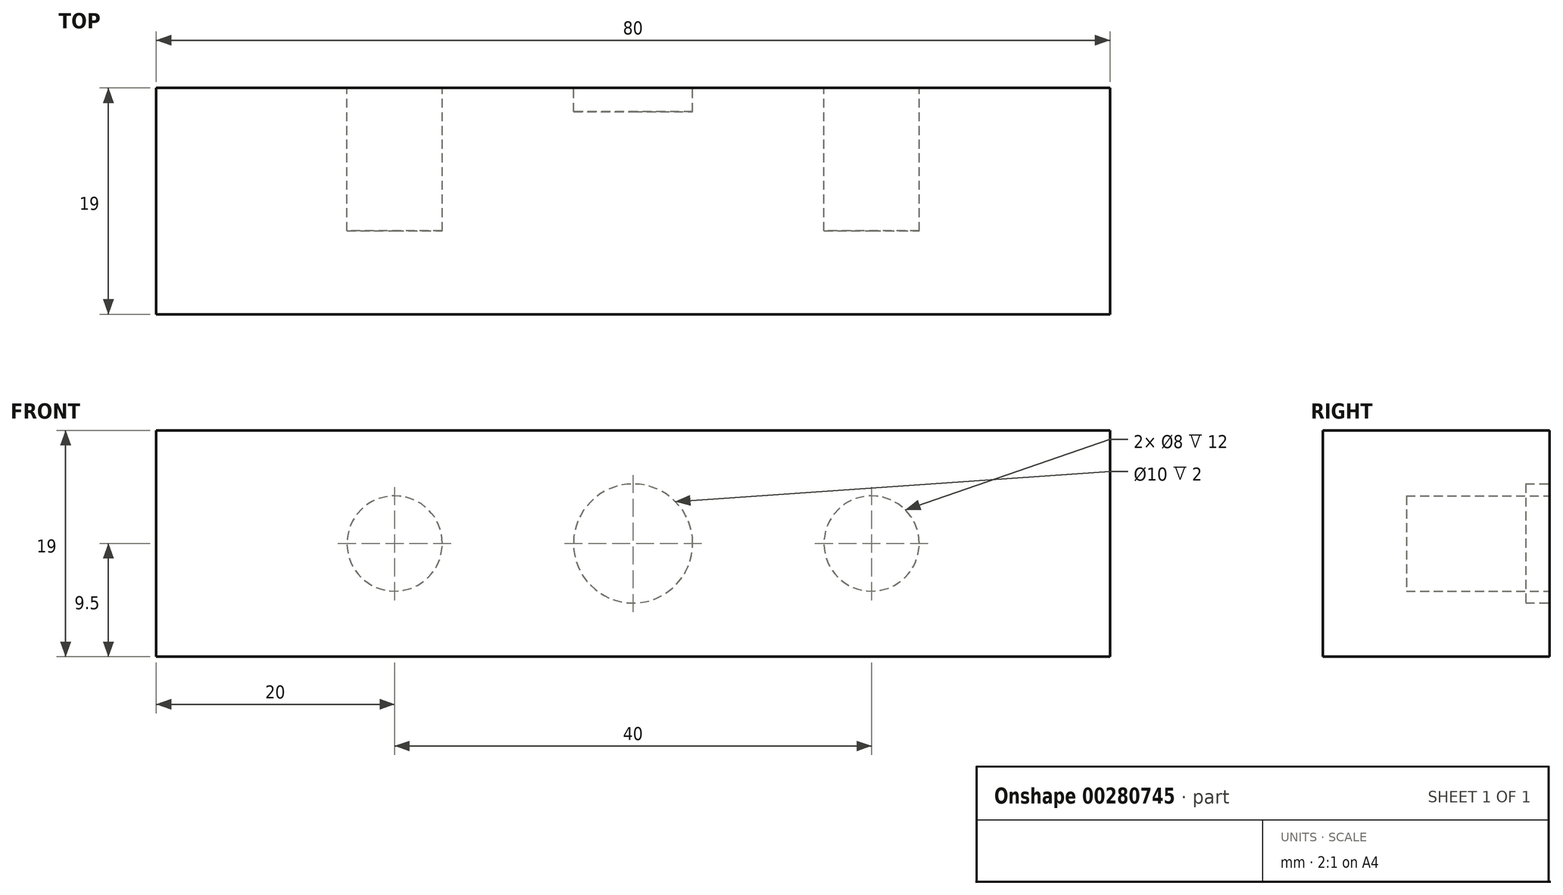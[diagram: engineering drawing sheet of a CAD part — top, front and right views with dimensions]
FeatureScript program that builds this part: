
annotation { "Feature Type Name" : "Feature", "Feature Type Description" : "" }
export const myFeature = defineFeature(function(context is Context, id is Id, definition is map)
    precondition{}
    {
        {
            var Q0;
            Q0=qCreatedBy(makeId("Top.planeOp"),FACE);
            var sketch = newSketch(context, id + "F0", { "sketchPlane" : qUnion([Q0])});
            skLineSegment(sketch, "E0.bottom", {"start": v(40, -9.5) * mm, "end": v(-40, -9.5) * mm});
            skLineSegment(sketch, "E0.top", {"start": v(40, 9.5) * mm, "end": v(-40, 9.5) * mm});
            skLineSegment(sketch, "E0.left", {"start": v(40, -9.5) * mm, "end": v(40, 9.5) * mm});
            skLineSegment(sketch, "E0.right", {"start": v(-40, -9.5) * mm, "end": v(-40, 9.5) * mm});
            skPoint(sketch, "E0.middle", {"position": v(0, 0) * mm});
            skSolve(sketch);
        }
        {
            var Q0;
            Q0=makeQuery(id+"F0.imprint","IMPRINT",FACE,{"disambiguationData":[TD([[makeQuery(id+"F0.imprint","IMPRINT",EDGE,{"derivedFrom":sQuery(id+"F0.wireOp",EDGE,"E0.bottom")}),-1.0]])]});
            extrude(context, id + "F1", {"entities" : qUnion([Q0]), "depth" : 19 * mm});
        }
        {
            var Q0;
            Q0=makeQuery(id+"F1.opExtrude","SWEPT_FACE",FACE,{"disambiguationData":[OSD([sQuery(id+"F0.wireOp",EDGE,"E0.top")])]});
            var sketch = newSketch(context, id + "F2", { "sketchPlane" : qUnion([Q0])});
            skLineSegment(sketch, "E1", {"start": v(-40, 9.5) * mm, "end": v(40, 9.5) * mm, "construction": true});
            skLineSegment(sketch, "E2", {"start": v(-30, 19) * mm, "end": v(-30, 0) * mm, "construction": true});
            skLineSegment(sketch, "E3", {"start": v(-10, 19) * mm, "end": v(-10, 0) * mm, "construction": true});
            skLineSegment(sketch, "E4", {"start": v(10, 19) * mm, "end": v(10, 0) * mm, "construction": true});
            skLineSegment(sketch, "E5", {"start": v(30, 19) * mm, "end": v(30, 0) * mm, "construction": true});
            skLineSegment(sketch, "E6", {"start": v(10, 19) * mm, "end": v(30, 0) * mm, "construction": true});
            skLineSegment(sketch, "E7", {"start": v(-10, 19) * mm, "end": v(-30, 0) * mm, "construction": true});
            skCircle(sketch, "E8", {"center": v(-20, 9.5) * mm, "radius": 4 * mm});
            skCircle(sketch, "E9", {"center": v(20, 9.5) * mm, "radius": 4 * mm});
            skCircle(sketch, "E10", {"center": v(0, 9.5) * mm, "radius": 5 * mm});
            skSolve(sketch);
        }
        {
            var Q0;
            Q0=makeQuery(id+"F2.imprint","IMPRINT",FACE,{"disambiguationData":[TD([[makeQuery(id+"F2.imprint","IMPRINT",EDGE,{"derivedFrom":sQuery(id+"F2.wireOp",EDGE,"E9")}),1.0]])]});
            var Q1;
            Q1=makeQuery(id+"F2.imprint","IMPRINT",FACE,{"disambiguationData":[TD([[makeQuery(id+"F2.imprint","IMPRINT",EDGE,{"derivedFrom":sQuery(id+"F2.wireOp",EDGE,"E8")}),1.0]])]});
            extrude(context, id + "F3", {"entities" : qUnion([Q0, Q1]), "operationType" : NewBodyOperationType.REMOVE, "oppositeDirection" : true, "depth" : 12 * mm});
        }
        {
            var Q0;
            Q0=makeQuery(id+"F2.imprint","IMPRINT",FACE,{"disambiguationData":[TD([[makeQuery(id+"F2.imprint","IMPRINT",EDGE,{"derivedFrom":sQuery(id+"F2.wireOp",EDGE,"E10")}),1.0]])]});
            extrude(context, id + "F4", {"entities" : qUnion([Q0]), "operationType" : NewBodyOperationType.REMOVE, "oppositeDirection" : true, "depth" : 2 * mm});
        }
    });
